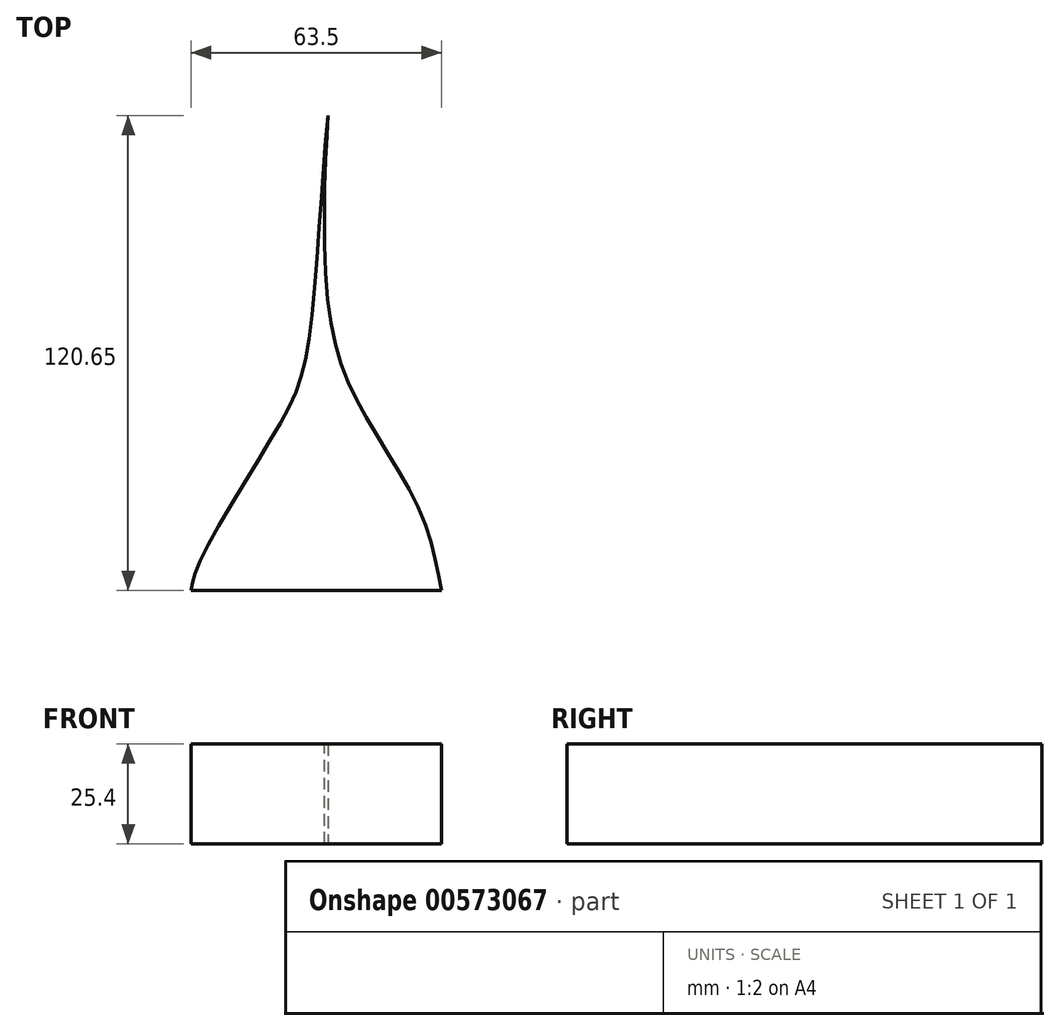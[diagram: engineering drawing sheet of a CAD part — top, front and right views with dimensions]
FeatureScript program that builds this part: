
annotation { "Feature Type Name" : "Feature", "Feature Type Description" : "" }
export const myFeature = defineFeature(function(context is Context, id is Id, definition is map)
    precondition{}
    {
        {
            var Q0;
            Q0=qCreatedBy(makeId("Top.planeOp"),FACE);
            var sketch = newSketch(context, id + "F0", { "sketchPlane" : qUnion([Q0])});
            skFitSpline(sketch, "E0", {"points": [v(0, 120.65) * mm, v(-4.96, 63) * mm, v(-12.9, 41.18) * mm, v(-32.5, 7.44) * mm, v(-34.73, 0) * mm], "startDerivative": vector(-14.68, -130.99) * mm, "endDerivative": vector(-6.63, -42.6) * mm});
            skFitSpline(sketch, "E1", {"points": [v(0, 120.65) * mm, v(0, 73.17) * mm, v(8.93, 45.4) * mm, v(23.56, 19.6) * mm, v(28.77, 0) * mm], "startDerivative": vector(-6.77, -104.5) * mm, "endDerivative": vector(15.22, -87.74) * mm});
            skLineSegment(sketch, "E2", {"start": v(-34.73, 0) * mm, "end": v(28.77, 0) * mm});
            skSolve(sketch);
        }
        {
            var Q0;
            Q0 = qSketchRegion(id + "F0", true);
            extrude(context, id + "F1", {"entities" : qUnion([Q0]), "depth" : 25.4 * mm, "offsetDistance" : 25.4 * mm});
        }
    });
